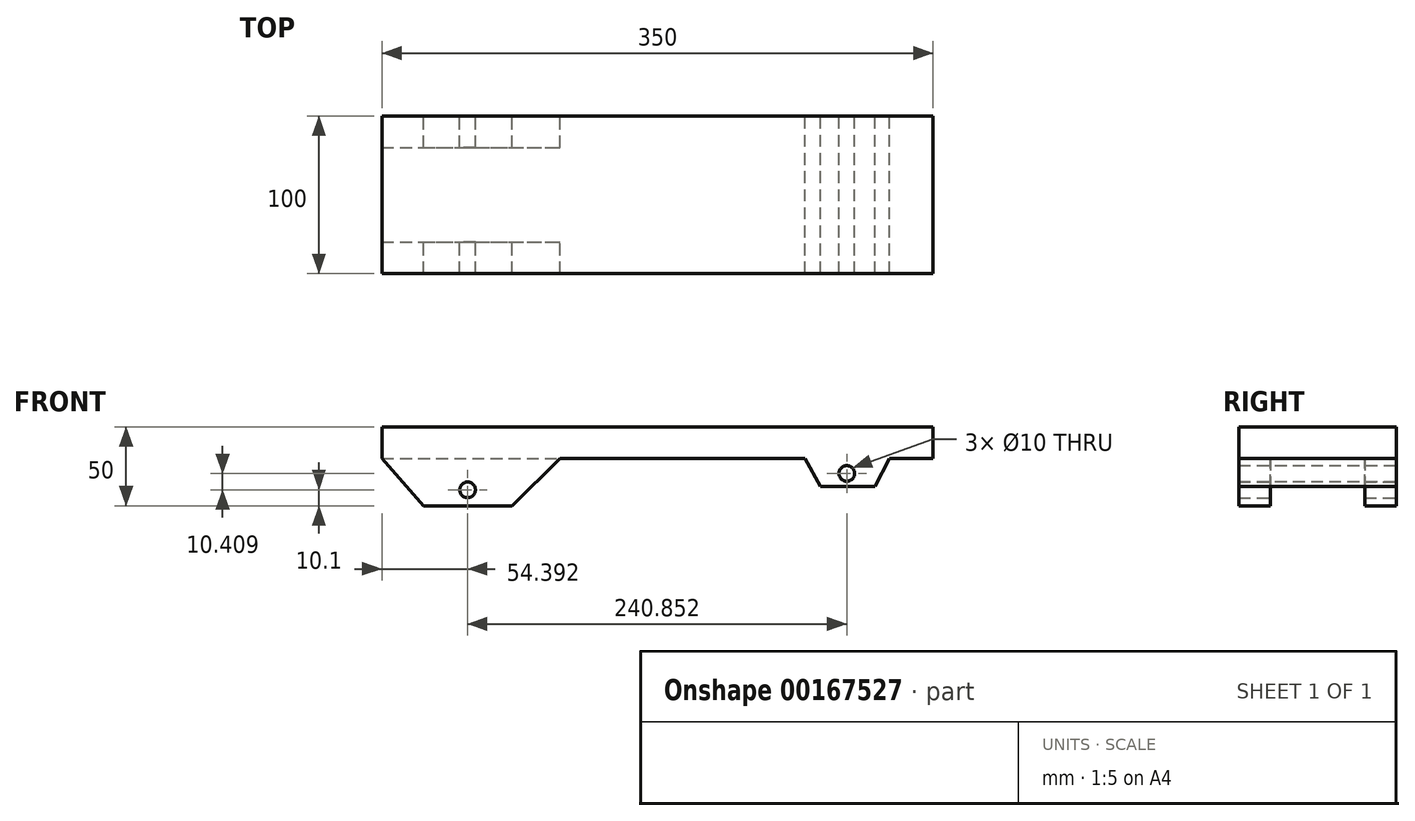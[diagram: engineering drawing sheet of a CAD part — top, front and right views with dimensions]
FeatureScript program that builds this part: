
annotation { "Feature Type Name" : "Feature", "Feature Type Description" : "" }
export const myFeature = defineFeature(function(context is Context, id is Id, definition is map)
    precondition{}
    {
        {
            var Q0;
            Q0=qCreatedBy(makeId("Front.planeOp"),FACE);
            var sketch = newSketch(context, id + "F0", { "sketchPlane" : qUnion([Q0])});
            skLineSegment(sketch, "E0.bottom", {"start": v(-131.64, 0) * mm, "end": v(218.36, 0) * mm});
            skLineSegment(sketch, "E0.top", {"start": v(-131.64, 20) * mm, "end": v(218.36, 20) * mm});
            skLineSegment(sketch, "E0.left", {"start": v(-131.64, 0) * mm, "end": v(-131.64, 20) * mm});
            skLineSegment(sketch, "E0.right", {"start": v(218.36, 0) * mm, "end": v(218.36, 20) * mm});
            skLineSegment(sketch, "E1.bottom", {"start": v(-131.64, 20) * mm, "end": v(-111.64, 20) * mm});
            skLineSegment(sketch, "E1.top", {"start": v(-131.64, 40) * mm, "end": v(-111.64, 40) * mm});
            skLineSegment(sketch, "E1.left", {"start": v(-131.64, 20) * mm, "end": v(-131.64, 40) * mm});
            skLineSegment(sketch, "E1.right", {"start": v(-111.64, 20) * mm, "end": v(-111.64, 40) * mm});
            skLineSegment(sketch, "E2.bottom", {"start": v(218.36, 20) * mm, "end": v(198.36, 20) * mm});
            skLineSegment(sketch, "E2.top", {"start": v(218.36, 60) * mm, "end": v(198.36, 60) * mm});
            skLineSegment(sketch, "E2.left", {"start": v(218.36, 20) * mm, "end": v(218.36, 60) * mm});
            skLineSegment(sketch, "E2.right", {"start": v(198.36, 20) * mm, "end": v(198.36, 60) * mm});
            skCircle(sketch, "E3", {"center": v(-121.64, 30) * mm, "radius": 5 * mm});
            skPoint(sketch, "E3.centerSnap0", {"position": v(-131.64, 30) * mm});
            skPoint(sketch, "E3.centerSnap1", {"position": v(-121.64, 20) * mm});
            skCircle(sketch, "E4", {"center": v(208.36, 51.05) * mm, "radius": 5 * mm});
            skPoint(sketch, "E4.centerSnap1", {"position": v(208.36, 20) * mm});
            skLineSegment(sketch, "E5", {"start": v(-131.64, 0) * mm, "end": v(-105.34, -30) * mm});
            skLineSegment(sketch, "E6", {"start": v(-105.34, -30) * mm, "end": v(-49.16, -30) * mm});
            skLineSegment(sketch, "E7", {"start": v(-49.16, -30) * mm, "end": v(-18.58, 0) * mm});
            skLineSegment(sketch, "E8", {"start": v(190.58, 0) * mm, "end": v(181.54, -17.74) * mm});
            skLineSegment(sketch, "E9", {"start": v(181.54, -17.74) * mm, "end": v(146.94, -17.74) * mm});
            skLineSegment(sketch, "E10", {"start": v(146.94, -17.74) * mm, "end": v(137.07, 0) * mm});
            skCircle(sketch, "E11", {"center": v(-77.25, -19.9) * mm, "radius": 5 * mm});
            skPoint(sketch, "E11.centerSnap0", {"position": v(-77.25, -30) * mm});
            skCircle(sketch, "E12", {"center": v(163.6, -9.5) * mm, "radius": 5 * mm});
            skSolve(sketch);
        }
        {
            var Q0;
            Q0=makeQuery(id+"F0.imprint","IMPRINT",FACE,{"disambiguationData":[TD([[makeQuery(id+"F0.imprint","IMPRINT",EDGE,{"derivedFrom":sQuery(id+"F0.wireOp",EDGE,"E0.bottom")}),1.0]])]});
            var Q1;
            Q1=makeQuery(id+"F0.imprint","IMPRINT",FACE,{"disambiguationData":[TD([[makeQuery(id+"F0.imprint","IMPRINT",EDGE,{"derivedFrom":sQuery(id+"F0.wireOp",EDGE,"E1.bottom")}),1.0]])]});
            var Q2;
            Q2=makeQuery(id+"F0.imprint","IMPRINT",FACE,{"disambiguationData":[TD([[makeQuery(id+"F0.imprint","IMPRINT",EDGE,{"derivedFrom":sQuery(id+"F0.wireOp",EDGE,"E2.bottom")}),-1.0]])]});
            var Q3;
            Q3=makeQuery(id+"F0.imprint","IMPRINT",FACE,{"disambiguationData":[TD([[makeQuery(id+"F0.imprint","IMPRINT",EDGE,{"derivedFrom":sQuery(id+"F0.wireOp",EDGE,"24475e39-1628-49d4-98f8-4ffff0ae0a2c.top")}),-1.0]])]});
            var Q4;
            {var subQ1=sQuery(id+"F0.wireOp",EDGE,"E8");Q4=makeQuery(id+"F0.imprint","IMPRINT",FACE,{"disambiguationData":[TD([[makeQuery(id+"F0.imprint","IMPRINT",EDGE,{"derivedFrom":subQ1}),-1.0]])]});}
            var Q5;
            {var subQ1=sQuery(id+"F0.wireOp",EDGE,"E5");Q5=makeQuery(id+"F0.imprint","IMPRINT",FACE,{"disambiguationData":[TD([[makeQuery(id+"F0.imprint","IMPRINT",EDGE,{"derivedFrom":subQ1}),1.0]])]});}
            extrude(context, id + "F1", {"entities" : qUnion([Q0, Q1, Q2, Q3, Q4, Q5]), "depth" : 100 * mm});
        }
        {
            var Q0;
            Q0=qCreatedBy(makeId("Right.planeOp"),FACE);
            var sketch = newSketch(context, id + "F2", { "sketchPlane" : qUnion([Q0])});
            skLineSegment(sketch, "E13.bottom", {"start": v(-20, 0) * mm, "end": v(-80, 0) * mm});
            skLineSegment(sketch, "E13.top", {"start": v(-20, -34.6) * mm, "end": v(-80, -34.6) * mm});
            skLineSegment(sketch, "E13.left", {"start": v(-20, 0) * mm, "end": v(-20, -34.6) * mm});
            skLineSegment(sketch, "E13.right", {"start": v(-80, 0) * mm, "end": v(-80, -34.6) * mm});
            skSolve(sketch);
        }
        {
            var Q0;
            Q0=makeQuery(id+"F2.imprint","IMPRINT",FACE,{"disambiguationData":[TD([[makeQuery(id+"F2.imprint","IMPRINT",EDGE,{"derivedFrom":sQuery(id+"F2.wireOp",EDGE,"E13.bottom")}),1.0]])]});
            extrude(context, id + "F3", {"entities" : qUnion([Q0]), "operationType" : NewBodyOperationType.REMOVE, "endBound" : BoundingType.THROUGH_ALL, "oppositeDirection" : true, "depth" : 25 * mm});
        }
    });
